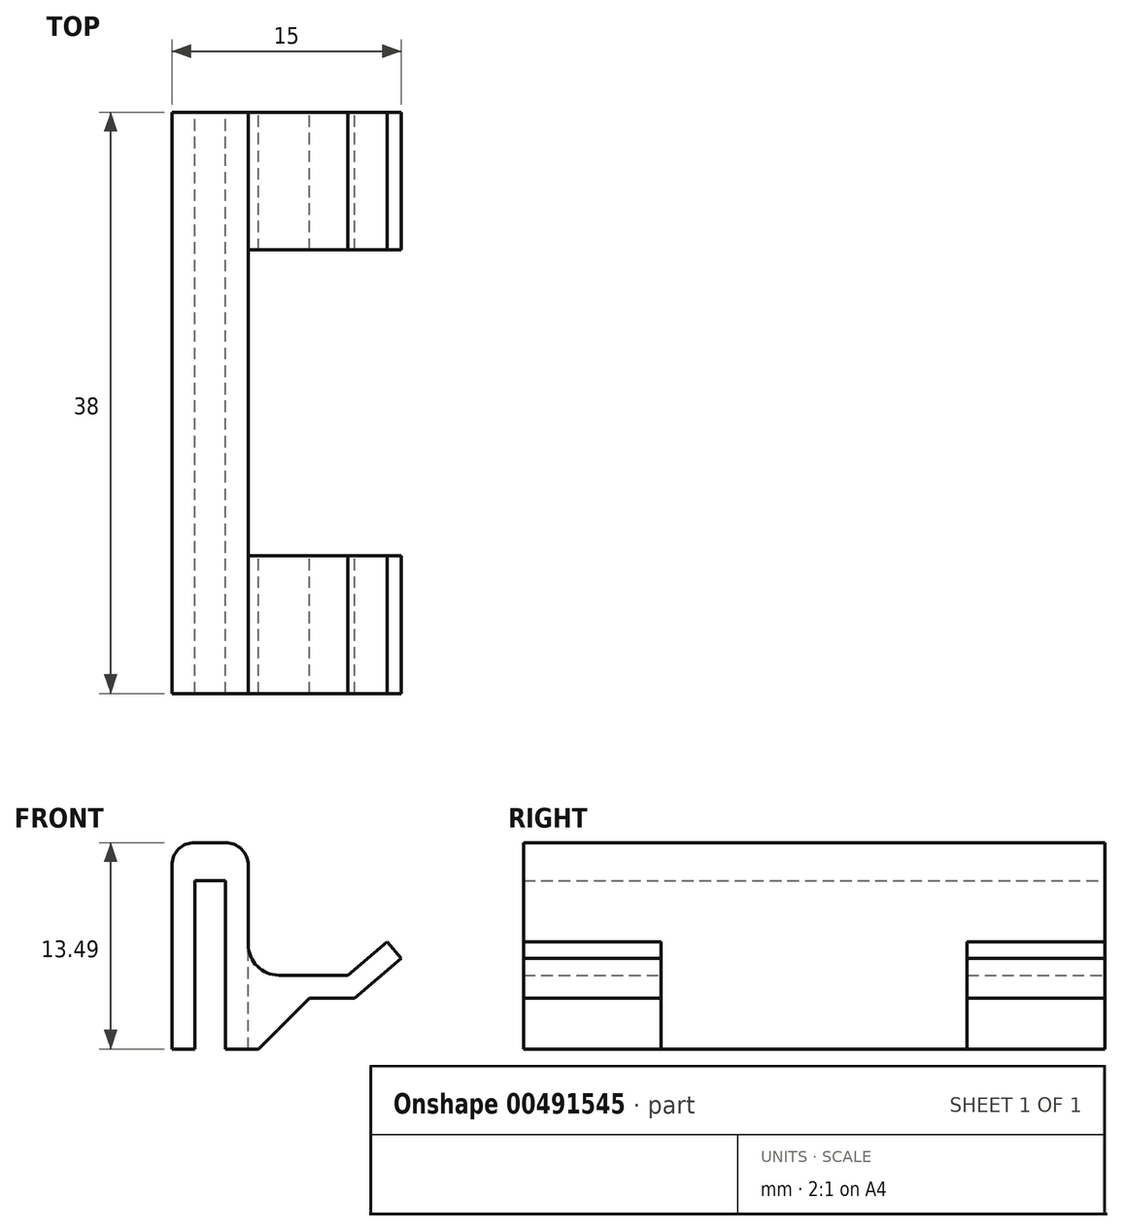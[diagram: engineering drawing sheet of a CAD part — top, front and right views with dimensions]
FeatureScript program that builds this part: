
annotation { "Feature Type Name" : "Feature", "Feature Type Description" : "" }
export const myFeature = defineFeature(function(context is Context, id is Id, definition is map)
    precondition{}
    {
        {
            var Q0;
            Q0=qCreatedBy(makeId("Front.planeOp"),FACE);
            var sketch = newSketch(context, id + "F0", { "sketchPlane" : qUnion([Q0])});
            skLineSegment(sketch, "E0", {"start": v(0, -11.09) * mm, "end": v(0, 16.91) * mm});
            skLineSegment(sketch, "E1", {"start": v(0, 16.91) * mm, "end": v(5, 16.91) * mm});
            skLineSegment(sketch, "E2", {"start": v(3.5, 14.41) * mm, "end": v(1.5, 14.41) * mm});
            skLineSegment(sketch, "E3", {"start": v(1.5, 14.41) * mm, "end": v(1.5, -11.09) * mm});
            skLineSegment(sketch, "E4", {"start": v(1.5, -11.09) * mm, "end": v(0, -11.09) * mm});
            skLineSegment(sketch, "E5", {"start": v(5, 8.25) * mm, "end": v(11.5, 8.25) * mm});
            skLineSegment(sketch, "E6", {"start": v(11.5, 8.25) * mm, "end": v(14.07, 10.44) * mm});
            skLineSegment(sketch, "E7", {"start": v(14.07, 10.44) * mm, "end": v(15, 9.34) * mm});
            skLineSegment(sketch, "E8", {"start": v(15, 9.34) * mm, "end": v(11.95, 6.75) * mm});
            skLineSegment(sketch, "E9", {"start": v(11.95, 6.75) * mm, "end": v(5, 6.75) * mm});
            skLineSegment(sketch, "E10", {"start": v(5, 16.91) * mm, "end": v(5, 3.42) * mm});
            skLineSegment(sketch, "E11", {"start": v(5, 3.42) * mm, "end": v(3.5, 3.42) * mm});
            skLineSegment(sketch, "E12", {"start": v(3.5, 3.42) * mm, "end": v(3.5, 14.41) * mm});
            skSolve(sketch);
        }
        {
            var Q0;
            Q0=makeQuery(id+"F0.imprint","IMPRINT",FACE,{"disambiguationData":[TD([[makeQuery(id+"F0.imprint","IMPRINT",EDGE,{"derivedFrom":sQuery(id+"F0.wireOp",EDGE,"E0")}),-1.0]])]});
            var Q1;
            {var subQ0=sQuery(id+"F0.wireOp",EDGE,"E5");Q1=makeQuery(id+"F0.imprint","IMPRINT",FACE,{"disambiguationData":[TD([[makeQuery(id+"F0.imprint","IMPRINT",EDGE,{"derivedFrom":subQ0}),-1.0]])]});}
            extrude(context, id + "F1", {"entities" : qUnion([Q0, Q1]), "depth" : 38 * mm});
        }
        {
            var Q0;
            Q0=makeQuery(id+"F1.opExtrude","SWEPT_FACE",FACE,{"disambiguationData":[OSD([sQuery(id+"F0.wireOp",EDGE,"E1")])]});
            var sketch = newSketch(context, id + "F2", { "sketchPlane" : qUnion([Q0])});
            skLineSegment(sketch, "E13", {"start": v(0, -19) * mm, "end": v(16.58, -19) * mm, "construction": true});
            skPoint(sketch, "E13.endSnap0", {"position": v(0, -19) * mm});
            skLineSegment(sketch, "E14", {"start": v(16.58, -19) * mm, "end": v(16.58, -9) * mm});
            skLineSegment(sketch, "E15", {"start": v(16.58, -9) * mm, "end": v(0, -9) * mm});
            skLineSegment(sketch, "E16", {"start": v(0, -9) * mm, "end": v(0, -19) * mm});
            skLineSegment(sketch, "E17.MirrorCS", {"start": v(0, -29) * mm, "end": v(0, -19) * mm});
            skLineSegment(sketch, "E18.MirrorCS", {"start": v(16.58, -19) * mm, "end": v(16.58, -29) * mm});
            skLineSegment(sketch, "E19.MirrorCS", {"start": v(16.58, -29) * mm, "end": v(0, -29) * mm});
            skSolve(sketch);
        }
        {
            var Q0;
            Q0=makeQuery(id+"F2.imprint","IMPRINT",FACE,{"disambiguationData":[TD([[makeQuery(id+"F2.imprint","IMPRINT",EDGE,{"derivedFrom":sQuery(id+"F2.wireOp",EDGE,"E14")}),1.0]])]});
            extrude(context, id + "F3", {"entities" : qUnion([Q0]), "operationType" : NewBodyOperationType.REMOVE, "oppositeDirection" : true, "depth" : 50 * mm});
        }
        {
            var Q0;
            {var subQ0=sQuery(id+"F0.wireOp",EDGE,"E10");var subQ1=sQuery(id+"F0.wireOp",EDGE,"E9");Q0=makeQuery(id+"F3.boolean.opBoolean","SPLIT",EDGE,{"disambiguationData":[TD([makeQuery(id+"F3.opExtrude","SWEPT_FACE",FACE,{"disambiguationData":[OSD([sQuery(id+"F2.wireOp",EDGE,"E19.MirrorCS")])]})])],"derivedFrom":makeQuery(id+"F1.opExtrude","SWEPT_EDGE",EDGE,{"disambiguationData":[OSD([subQ1,subQ0])]})});}
            var Q1;
            {var subQ0=sQuery(id+"F0.wireOp",EDGE,"E10");var subQ1=sQuery(id+"F0.wireOp",EDGE,"E9");Q1=makeQuery(id+"F3.boolean.opBoolean","SPLIT",EDGE,{"disambiguationData":[TD([makeQuery(id+"F3.opExtrude","SWEPT_FACE",FACE,{"disambiguationData":[OSD([sQuery(id+"F2.wireOp",EDGE,"E15")])]})])],"derivedFrom":makeQuery(id+"F1.opExtrude","SWEPT_EDGE",EDGE,{"disambiguationData":[OSD([subQ1,subQ0])]})});}
            chamfer(context, id + "F4", {"entities" : qUnion([Q0, Q1]), "width" : 4 * mm, "tangentPropagation" : true});
        }
        {
            var Q0;
            Q0=makeQuery(id+"F1.opExtrude","SWEPT_FACE",FACE,{"disambiguationData":[OSD([sQuery(id+"F0.wireOp",EDGE,"E3")])]});
            var sketch = newSketch(context, id + "F5", { "sketchPlane" : qUnion([Q0])});
            skLineSegment(sketch, "E20.0.1", {"start": v(0, 14.41) * mm, "end": v(-38, 14.41) * mm});
            skLineSegment(sketch, "E20.0.2", {"start": v(-38, 14.41) * mm, "end": v(-38, -11.09) * mm});
            skLineSegment(sketch, "E20.0.3", {"start": v(-38, -11.09) * mm, "end": v(0, -11.09) * mm});
            skPoint(sketch, "E21.0", {"position": v(-38, 3.42) * mm});
            skPoint(sketch, "E22.0", {"position": v(0, 3.42) * mm});
            skLineSegment(sketch, "E23.0.0", {"start": v(0, -11.09) * mm, "end": v(0, 14.41) * mm});
            skLineSegment(sketch, "E24.bottom", {"start": v(-38, 3.42) * mm, "end": v(0, 3.42) * mm});
            skLineSegment(sketch, "E24.left", {"start": v(-38, 3.42) * mm, "end": v(-38, -11.09) * mm});
            skLineSegment(sketch, "E24.right", {"start": v(0, 3.42) * mm, "end": v(0, -11.09) * mm});
            skSolve(sketch);
        }
        {
            var Q0;
            Q0=makeQuery(id+"F5.imprint","IMPRINT",FACE,{"disambiguationData":[TD([[makeQuery(id+"F5.imprint","IMPRINT",EDGE,{"derivedFrom":sQuery(id+"F5.wireOp",EDGE,"E24.bottom")}),-1.0]])]});
            extrude(context, id + "F6", {"entities" : qUnion([Q0]), "operationType" : NewBodyOperationType.REMOVE, "oppositeDirection" : true, "depth" : 25 * mm});
        }
        {
            var Q0;
            {var subQ0=sQuery(id+"F0.wireOp",EDGE,"E10");var subQ3=sQuery(id+"F0.wireOp",EDGE,"E5");Q0=makeQuery(id+"F3.boolean.opBoolean","SPLIT",EDGE,{"disambiguationData":[TD([makeQuery(id+"F3.opExtrude","SWEPT_FACE",FACE,{"disambiguationData":[OSD([sQuery(id+"F2.wireOp",EDGE,"E19.MirrorCS")])]})])],"derivedFrom":makeQuery(id+"F1.opExtrude","SWEPT_EDGE",EDGE,{"disambiguationData":[OSD([subQ3,subQ0])]})});}
            var Q1;
            {var subQ0=sQuery(id+"F0.wireOp",EDGE,"E10");var subQ4=sQuery(id+"F0.wireOp",EDGE,"E5");Q1=makeQuery(id+"F3.boolean.opBoolean","SPLIT",EDGE,{"disambiguationData":[TD([makeQuery(id+"F3.opExtrude","SWEPT_FACE",FACE,{"disambiguationData":[OSD([sQuery(id+"F2.wireOp",EDGE,"E15")])]})])],"derivedFrom":makeQuery(id+"F1.opExtrude","SWEPT_EDGE",EDGE,{"disambiguationData":[OSD([subQ4,subQ0])]})});}
            fillet(context, id + "F7", {"entities" : qUnion([Q0, Q1]), "radius" : 2 * mm, "tangentPropagation" : true, "allowEdgeOverflow" : false});
        }
        {
            var Q0;
            Q0=makeQuery(id+"F1.opExtrude","SWEPT_EDGE",EDGE,{"disambiguationData":[OSD([sQuery(id+"F0.wireOp",EDGE,"E1"),sQuery(id+"F0.wireOp",EDGE,"E10")])]});
            var Q1;
            Q1=makeQuery(id+"F1.opExtrude","SWEPT_EDGE",EDGE,{"disambiguationData":[OSD([sQuery(id+"F0.wireOp",EDGE,"E0"),sQuery(id+"F0.wireOp",EDGE,"E1")])]});
            fillet(context, id + "F8", {"entities" : qUnion([Q0, Q1]), "radius" : 1.5 * mm, "tangentPropagation" : true, "allowEdgeOverflow" : false});
        }
    });
